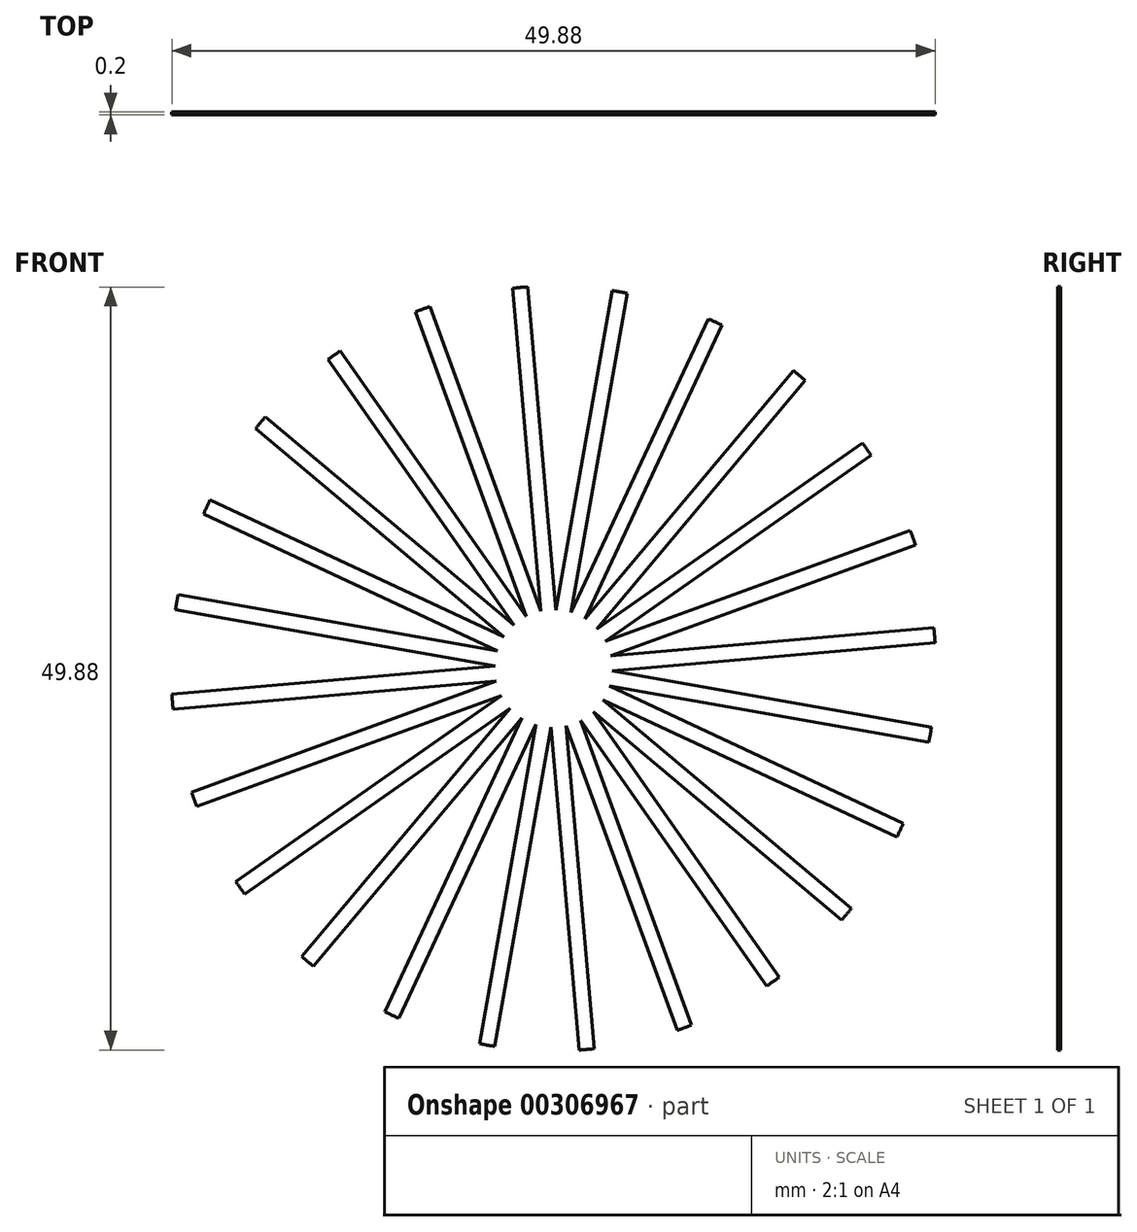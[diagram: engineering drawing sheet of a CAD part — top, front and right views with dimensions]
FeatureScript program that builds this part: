
annotation { "Feature Type Name" : "Feature", "Feature Type Description" : "" }
export const myFeature = defineFeature(function(context is Context, id is Id, definition is map)
    precondition{}
    {
        {
            var Q0;
            Q0=qCreatedBy(makeId("Front.planeOp"),FACE);
            var sketch = newSketch(context, id + "F0", { "sketchPlane" : qUnion([Q0])});
            skCircle(sketch, "E0", {"center": v(0, 0) * mm, "radius": 25 * mm});
            skLineSegment(sketch, "E1", {"start": v(0, 0) * mm, "end": v(11.49, 65.16) * mm, "construction": true});
            skLineSegment(sketch, "E2", {"start": v(0, 2.88) * mm, "end": v(3.85, 24.7) * mm});
            skLineSegment(sketch, "E3", {"start": v(0.5, 0) * mm, "end": v(4.83, 24.53) * mm});
            skLineSegment(sketch, "E4", {"start": v(0, 2.88) * mm, "end": v(0.5, 0) * mm});
            skLineSegment(sketch, "E5.1.0", {"start": v(-0.75, 2.78) * mm, "end": v(-2.68, 24.86) * mm});
            skLineSegment(sketch, "E5.1.1", {"start": v(0.5, 0.13) * mm, "end": v(-1.68, 24.94) * mm});
            skLineSegment(sketch, "E5.2.0", {"start": v(-1.44, 2.5) * mm, "end": v(-9.02, 23.32) * mm});
            skLineSegment(sketch, "E5.2.1", {"start": v(0.44, 0.25) * mm, "end": v(-8.08, 23.66) * mm});
            skLineSegment(sketch, "E6.1.3.0", {"start": v(-2.04, 2.04) * mm, "end": v(-14.75, 20.19) * mm});
            skLineSegment(sketch, "E6.3.3.0", {"start": v(0.36, 0.36) * mm, "end": v(-13.93, 20.76) * mm});
            skLineSegment(sketch, "E6.1.4.0", {"start": v(-2.5, 1.44) * mm, "end": v(-19.47, 15.68) * mm});
            skLineSegment(sketch, "E6.3.4.0", {"start": v(0.25, 0.44) * mm, "end": v(-18.83, 16.45) * mm});
            skLineSegment(sketch, "E6.1.5.0", {"start": v(-2.78, 0.75) * mm, "end": v(-22.86, 10.11) * mm});
            skLineSegment(sketch, "E6.3.5.0", {"start": v(0.13, 0.5) * mm, "end": v(-22.44, 11.02) * mm});
            skLineSegment(sketch, "E6.1.6.0", {"start": v(-2.88, 0) * mm, "end": v(-24.7, 3.85) * mm});
            skLineSegment(sketch, "E6.3.6.0", {"start": v(0, 0.5) * mm, "end": v(-24.53, 4.83) * mm});
            skLineSegment(sketch, "E6.1.7.0", {"start": v(-2.78, -0.75) * mm, "end": v(-24.86, -2.68) * mm});
            skLineSegment(sketch, "E6.3.7.0", {"start": v(-0.13, 0.5) * mm, "end": v(-24.94, -1.68) * mm});
            skLineSegment(sketch, "E6.1.8.0", {"start": v(-2.5, -1.44) * mm, "end": v(-23.32, -9.02) * mm});
            skLineSegment(sketch, "E6.3.8.0", {"start": v(-0.25, 0.44) * mm, "end": v(-23.66, -8.08) * mm});
            skLineSegment(sketch, "E6.1.9.0", {"start": v(-2.04, -2.04) * mm, "end": v(-20.19, -14.75) * mm});
            skLineSegment(sketch, "E6.3.9.0", {"start": v(-0.36, 0.36) * mm, "end": v(-20.76, -13.93) * mm});
            skLineSegment(sketch, "E6.1.10.0", {"start": v(-1.44, -2.5) * mm, "end": v(-15.68, -19.47) * mm});
            skLineSegment(sketch, "E6.3.10.0", {"start": v(-0.44, 0.25) * mm, "end": v(-16.45, -18.83) * mm});
            skLineSegment(sketch, "E6.1.11.0", {"start": v(-0.75, -2.78) * mm, "end": v(-10.11, -22.86) * mm});
            skLineSegment(sketch, "E6.3.11.0", {"start": v(-0.5, 0.13) * mm, "end": v(-11.02, -22.44) * mm});
            skLineSegment(sketch, "E6.1.12.0", {"start": v(0, -2.88) * mm, "end": v(-3.85, -24.7) * mm});
            skLineSegment(sketch, "E6.3.12.0", {"start": v(-0.5, 0) * mm, "end": v(-4.83, -24.53) * mm});
            skLineSegment(sketch, "E6.1.13.0", {"start": v(0.75, -2.78) * mm, "end": v(2.68, -24.86) * mm});
            skLineSegment(sketch, "E6.3.13.0", {"start": v(-0.5, -0.13) * mm, "end": v(1.68, -24.94) * mm});
            skLineSegment(sketch, "E6.1.14.0", {"start": v(1.44, -2.5) * mm, "end": v(9.02, -23.32) * mm});
            skLineSegment(sketch, "E6.3.14.0", {"start": v(-0.44, -0.25) * mm, "end": v(8.08, -23.66) * mm});
            skLineSegment(sketch, "E6.1.15.0", {"start": v(2.04, -2.04) * mm, "end": v(14.75, -20.19) * mm});
            skLineSegment(sketch, "E6.3.15.0", {"start": v(-0.36, -0.36) * mm, "end": v(13.93, -20.76) * mm});
            skLineSegment(sketch, "E6.1.16.0", {"start": v(2.5, -1.44) * mm, "end": v(19.47, -15.68) * mm});
            skLineSegment(sketch, "E6.3.16.0", {"start": v(-0.25, -0.44) * mm, "end": v(18.83, -16.45) * mm});
            skLineSegment(sketch, "E6.1.17.0", {"start": v(2.78, -0.75) * mm, "end": v(22.86, -10.11) * mm});
            skLineSegment(sketch, "E6.3.17.0", {"start": v(-0.13, -0.5) * mm, "end": v(22.44, -11.02) * mm});
            skLineSegment(sketch, "E6.1.18.0", {"start": v(2.88, 0) * mm, "end": v(24.7, -3.85) * mm});
            skLineSegment(sketch, "E6.3.18.0", {"start": v(0, -0.5) * mm, "end": v(24.53, -4.83) * mm});
            skLineSegment(sketch, "E6.1.19.0", {"start": v(2.78, 0.75) * mm, "end": v(24.86, 2.68) * mm});
            skLineSegment(sketch, "E6.3.19.0", {"start": v(0.13, -0.5) * mm, "end": v(24.94, 1.68) * mm});
            skLineSegment(sketch, "E6.1.20.0", {"start": v(2.5, 1.44) * mm, "end": v(23.32, 9.02) * mm});
            skLineSegment(sketch, "E6.3.20.0", {"start": v(0.25, -0.44) * mm, "end": v(23.66, 8.08) * mm});
            skLineSegment(sketch, "E6.1.21.0", {"start": v(2.04, 2.04) * mm, "end": v(20.19, 14.75) * mm});
            skLineSegment(sketch, "E6.3.21.0", {"start": v(0.36, -0.36) * mm, "end": v(20.76, 13.93) * mm});
            skLineSegment(sketch, "E6.1.22.0", {"start": v(1.44, 2.5) * mm, "end": v(15.68, 19.47) * mm});
            skLineSegment(sketch, "E6.3.22.0", {"start": v(0.44, -0.25) * mm, "end": v(16.45, 18.83) * mm});
            skLineSegment(sketch, "E6.1.23.0", {"start": v(0.75, 2.78) * mm, "end": v(10.11, 22.86) * mm});
            skLineSegment(sketch, "E6.3.23.0", {"start": v(0.5, -0.13) * mm, "end": v(11.02, 22.44) * mm});
            skSolve(sketch);
        }
        {
            var Q0;
            {var subQ0=sQuery(id+"F0.wireOp",EDGE,"E6.1.4.0");var subQ1=sQuery(id+"F0.wireOp",EDGE,"E0");var subQ2=makeQuery(id+"F0.imprint","INTERSECT",VERTEX,{"derivedFrom":[subQ1,subQ0]});Q0=makeQuery(id+"F0.imprint","IMPRINT",FACE,{"disambiguationData":[TD([[makeQuery(id+"F0.imprint","IMPRINT",EDGE,{"disambiguationData":[TD([[subQ2,1.0]])],"derivedFrom":subQ1}),1.0]])]});}
            var Q1;
            {var subQ0=sQuery(id+"F0.wireOp",EDGE,"E6.1.3.0");var subQ1=sQuery(id+"F0.wireOp",EDGE,"E0");var subQ2=makeQuery(id+"F0.imprint","INTERSECT",VERTEX,{"derivedFrom":[subQ1,subQ0]});Q1=makeQuery(id+"F0.imprint","IMPRINT",FACE,{"disambiguationData":[TD([[makeQuery(id+"F0.imprint","IMPRINT",EDGE,{"disambiguationData":[TD([[subQ2,1.0]])],"derivedFrom":subQ1}),1.0]])]});}
            var Q2;
            {var subQ0=sQuery(id+"F0.wireOp",EDGE,"E5.2.0");var subQ1=sQuery(id+"F0.wireOp",EDGE,"E0");var subQ2=makeQuery(id+"F0.imprint","INTERSECT",VERTEX,{"derivedFrom":[subQ1,subQ0]});Q2=makeQuery(id+"F0.imprint","IMPRINT",FACE,{"disambiguationData":[TD([[makeQuery(id+"F0.imprint","IMPRINT",EDGE,{"disambiguationData":[TD([[subQ2,1.0]])],"derivedFrom":subQ1}),1.0]])]});}
            var Q3;
            {var subQ0=sQuery(id+"F0.wireOp",EDGE,"E5.1.0");var subQ1=sQuery(id+"F0.wireOp",EDGE,"E0");var subQ2=makeQuery(id+"F0.imprint","INTERSECT",VERTEX,{"derivedFrom":[subQ1,subQ0]});Q3=makeQuery(id+"F0.imprint","IMPRINT",FACE,{"disambiguationData":[TD([[makeQuery(id+"F0.imprint","IMPRINT",EDGE,{"disambiguationData":[TD([[subQ2,1.0]])],"derivedFrom":subQ1}),1.0]])]});}
            var Q4;
            {var subQ1=sQuery(id+"F0.wireOp",EDGE,"E2");var subQ5=sQuery(id+"F0.wireOp",EDGE,"E0");var subQ6=makeQuery(id+"F0.imprint","INTERSECT",VERTEX,{"derivedFrom":[subQ5,subQ1]});Q4=makeQuery(id+"F0.imprint","IMPRINT",FACE,{"disambiguationData":[TD([[makeQuery(id+"F0.imprint","IMPRINT",EDGE,{"disambiguationData":[TD([[subQ6,1.0]])],"derivedFrom":subQ5}),1.0]])]});}
            var Q5;
            {var subQ0=sQuery(id+"F0.wireOp",EDGE,"E6.1.23.0");var subQ1=sQuery(id+"F0.wireOp",EDGE,"E0");var subQ2=makeQuery(id+"F0.imprint","INTERSECT",VERTEX,{"derivedFrom":[subQ1,subQ0]});Q5=makeQuery(id+"F0.imprint","IMPRINT",FACE,{"disambiguationData":[TD([[makeQuery(id+"F0.imprint","IMPRINT",EDGE,{"disambiguationData":[TD([[subQ2,1.0]])],"derivedFrom":subQ1}),1.0]])]});}
            var Q6;
            {var subQ1=sQuery(id+"F0.wireOp",EDGE,"E0");var subQ7=sQuery(id+"F0.wireOp",EDGE,"E6.1.22.0");var subQ9=makeQuery(id+"F0.imprint","INTERSECT",VERTEX,{"derivedFrom":[subQ1,subQ7]});Q6=makeQuery(id+"F0.imprint","IMPRINT",FACE,{"disambiguationData":[TD([[makeQuery(id+"F0.imprint","IMPRINT",EDGE,{"disambiguationData":[TD([[subQ9,1.0]])],"derivedFrom":subQ1}),1.0]])]});}
            var Q7;
            {var subQ0=sQuery(id+"F0.wireOp",EDGE,"E6.1.21.0");var subQ1=sQuery(id+"F0.wireOp",EDGE,"E0");var subQ2=makeQuery(id+"F0.imprint","INTERSECT",VERTEX,{"derivedFrom":[subQ1,subQ0]});Q7=makeQuery(id+"F0.imprint","IMPRINT",FACE,{"disambiguationData":[TD([[makeQuery(id+"F0.imprint","IMPRINT",EDGE,{"disambiguationData":[TD([[subQ2,1.0]])],"derivedFrom":subQ1}),1.0]])]});}
            var Q8;
            {var subQ0=sQuery(id+"F0.wireOp",EDGE,"E6.1.19.0");var subQ1=sQuery(id+"F0.wireOp",EDGE,"E0");var subQ2=makeQuery(id+"F0.imprint","INTERSECT",VERTEX,{"derivedFrom":[subQ1,subQ0]});Q8=makeQuery(id+"F0.imprint","IMPRINT",FACE,{"disambiguationData":[TD([[makeQuery(id+"F0.imprint","IMPRINT",EDGE,{"disambiguationData":[TD([[subQ2,1.0]])],"derivedFrom":subQ1}),1.0]])]});}
            var Q9;
            {var subQ0=sQuery(id+"F0.wireOp",EDGE,"E6.1.18.0");var subQ1=sQuery(id+"F0.wireOp",EDGE,"E0");var subQ2=makeQuery(id+"F0.imprint","INTERSECT",VERTEX,{"derivedFrom":[subQ1,subQ0]});Q9=makeQuery(id+"F0.imprint","IMPRINT",FACE,{"disambiguationData":[TD([[makeQuery(id+"F0.imprint","IMPRINT",EDGE,{"disambiguationData":[TD([[subQ2,1.0]])],"derivedFrom":subQ1}),1.0]])]});}
            var Q10;
            {var subQ0=sQuery(id+"F0.wireOp",EDGE,"E6.1.17.0");var subQ1=sQuery(id+"F0.wireOp",EDGE,"E0");var subQ2=makeQuery(id+"F0.imprint","INTERSECT",VERTEX,{"derivedFrom":[subQ1,subQ0]});Q10=makeQuery(id+"F0.imprint","IMPRINT",FACE,{"disambiguationData":[TD([[makeQuery(id+"F0.imprint","IMPRINT",EDGE,{"disambiguationData":[TD([[subQ2,1.0]])],"derivedFrom":subQ1}),1.0]])]});}
            var Q11;
            {var subQ0=sQuery(id+"F0.wireOp",EDGE,"E6.1.16.0");var subQ1=sQuery(id+"F0.wireOp",EDGE,"E0");var subQ2=makeQuery(id+"F0.imprint","INTERSECT",VERTEX,{"derivedFrom":[subQ1,subQ0]});Q11=makeQuery(id+"F0.imprint","IMPRINT",FACE,{"disambiguationData":[TD([[makeQuery(id+"F0.imprint","IMPRINT",EDGE,{"disambiguationData":[TD([[subQ2,1.0]])],"derivedFrom":subQ1}),1.0]])]});}
            var Q12;
            {var subQ0=sQuery(id+"F0.wireOp",EDGE,"E6.1.15.0");var subQ1=sQuery(id+"F0.wireOp",EDGE,"E0");var subQ2=makeQuery(id+"F0.imprint","INTERSECT",VERTEX,{"derivedFrom":[subQ1,subQ0]});Q12=makeQuery(id+"F0.imprint","IMPRINT",FACE,{"disambiguationData":[TD([[makeQuery(id+"F0.imprint","IMPRINT",EDGE,{"disambiguationData":[TD([[subQ2,1.0]])],"derivedFrom":subQ1}),1.0]])]});}
            var Q13;
            {var subQ0=sQuery(id+"F0.wireOp",EDGE,"E6.1.14.0");var subQ1=sQuery(id+"F0.wireOp",EDGE,"E0");var subQ2=makeQuery(id+"F0.imprint","INTERSECT",VERTEX,{"derivedFrom":[subQ1,subQ0]});Q13=makeQuery(id+"F0.imprint","IMPRINT",FACE,{"disambiguationData":[TD([[makeQuery(id+"F0.imprint","IMPRINT",EDGE,{"disambiguationData":[TD([[subQ2,1.0]])],"derivedFrom":subQ1}),1.0]])]});}
            var Q14;
            {var subQ0=sQuery(id+"F0.wireOp",EDGE,"E6.1.13.0");var subQ1=sQuery(id+"F0.wireOp",EDGE,"E0");var subQ2=makeQuery(id+"F0.imprint","INTERSECT",VERTEX,{"derivedFrom":[subQ1,subQ0]});Q14=makeQuery(id+"F0.imprint","IMPRINT",FACE,{"disambiguationData":[TD([[makeQuery(id+"F0.imprint","IMPRINT",EDGE,{"disambiguationData":[TD([[subQ2,1.0]])],"derivedFrom":subQ1}),1.0]])]});}
            var Q15;
            {var subQ0=sQuery(id+"F0.wireOp",EDGE,"E6.1.12.0");var subQ1=sQuery(id+"F0.wireOp",EDGE,"E0");var subQ2=makeQuery(id+"F0.imprint","INTERSECT",VERTEX,{"derivedFrom":[subQ1,subQ0]});Q15=makeQuery(id+"F0.imprint","IMPRINT",FACE,{"disambiguationData":[TD([[makeQuery(id+"F0.imprint","IMPRINT",EDGE,{"disambiguationData":[TD([[subQ2,1.0]])],"derivedFrom":subQ1}),1.0]])]});}
            var Q16;
            {var subQ0=sQuery(id+"F0.wireOp",EDGE,"E6.1.11.0");var subQ1=sQuery(id+"F0.wireOp",EDGE,"E0");var subQ2=makeQuery(id+"F0.imprint","INTERSECT",VERTEX,{"derivedFrom":[subQ1,subQ0]});Q16=makeQuery(id+"F0.imprint","IMPRINT",FACE,{"disambiguationData":[TD([[makeQuery(id+"F0.imprint","IMPRINT",EDGE,{"disambiguationData":[TD([[subQ2,1.0]])],"derivedFrom":subQ1}),1.0]])]});}
            var Q17;
            {var subQ0=sQuery(id+"F0.wireOp",EDGE,"E6.1.10.0");var subQ1=sQuery(id+"F0.wireOp",EDGE,"E0");var subQ2=makeQuery(id+"F0.imprint","INTERSECT",VERTEX,{"derivedFrom":[subQ1,subQ0]});Q17=makeQuery(id+"F0.imprint","IMPRINT",FACE,{"disambiguationData":[TD([[makeQuery(id+"F0.imprint","IMPRINT",EDGE,{"disambiguationData":[TD([[subQ2,1.0]])],"derivedFrom":subQ1}),1.0]])]});}
            var Q18;
            {var subQ0=sQuery(id+"F0.wireOp",EDGE,"E6.1.9.0");var subQ1=sQuery(id+"F0.wireOp",EDGE,"E0");var subQ2=makeQuery(id+"F0.imprint","INTERSECT",VERTEX,{"derivedFrom":[subQ1,subQ0]});Q18=makeQuery(id+"F0.imprint","IMPRINT",FACE,{"disambiguationData":[TD([[makeQuery(id+"F0.imprint","IMPRINT",EDGE,{"disambiguationData":[TD([[subQ2,1.0]])],"derivedFrom":subQ1}),1.0]])]});}
            var Q19;
            {var subQ0=sQuery(id+"F0.wireOp",EDGE,"E6.1.8.0");var subQ1=sQuery(id+"F0.wireOp",EDGE,"E0");var subQ2=makeQuery(id+"F0.imprint","INTERSECT",VERTEX,{"derivedFrom":[subQ1,subQ0]});Q19=makeQuery(id+"F0.imprint","IMPRINT",FACE,{"disambiguationData":[TD([[makeQuery(id+"F0.imprint","IMPRINT",EDGE,{"disambiguationData":[TD([[subQ2,1.0]])],"derivedFrom":subQ1}),1.0]])]});}
            var Q20;
            {var subQ0=sQuery(id+"F0.wireOp",EDGE,"E6.1.7.0");var subQ1=sQuery(id+"F0.wireOp",EDGE,"E0");var subQ2=makeQuery(id+"F0.imprint","INTERSECT",VERTEX,{"derivedFrom":[subQ1,subQ0]});Q20=makeQuery(id+"F0.imprint","IMPRINT",FACE,{"disambiguationData":[TD([[makeQuery(id+"F0.imprint","IMPRINT",EDGE,{"disambiguationData":[TD([[subQ2,1.0]])],"derivedFrom":subQ1}),1.0]])]});}
            var Q21;
            {var subQ0=sQuery(id+"F0.wireOp",EDGE,"E6.1.6.0");var subQ1=sQuery(id+"F0.wireOp",EDGE,"E0");var subQ2=makeQuery(id+"F0.imprint","INTERSECT",VERTEX,{"derivedFrom":[subQ1,subQ0]});Q21=makeQuery(id+"F0.imprint","IMPRINT",FACE,{"disambiguationData":[TD([[makeQuery(id+"F0.imprint","IMPRINT",EDGE,{"disambiguationData":[TD([[subQ2,1.0]])],"derivedFrom":subQ1}),1.0]])]});}
            extrude(context, id + "F1", {"entities" : qUnion([Q0, Q1, Q2, Q3, Q4, Q5, Q6, Q7, Q8, Q9, Q10, Q11, Q12, Q13, Q14, Q15, Q16, Q17, Q18, Q19, Q20, Q21]), "depth" : .2 * mm});
        }
    });
